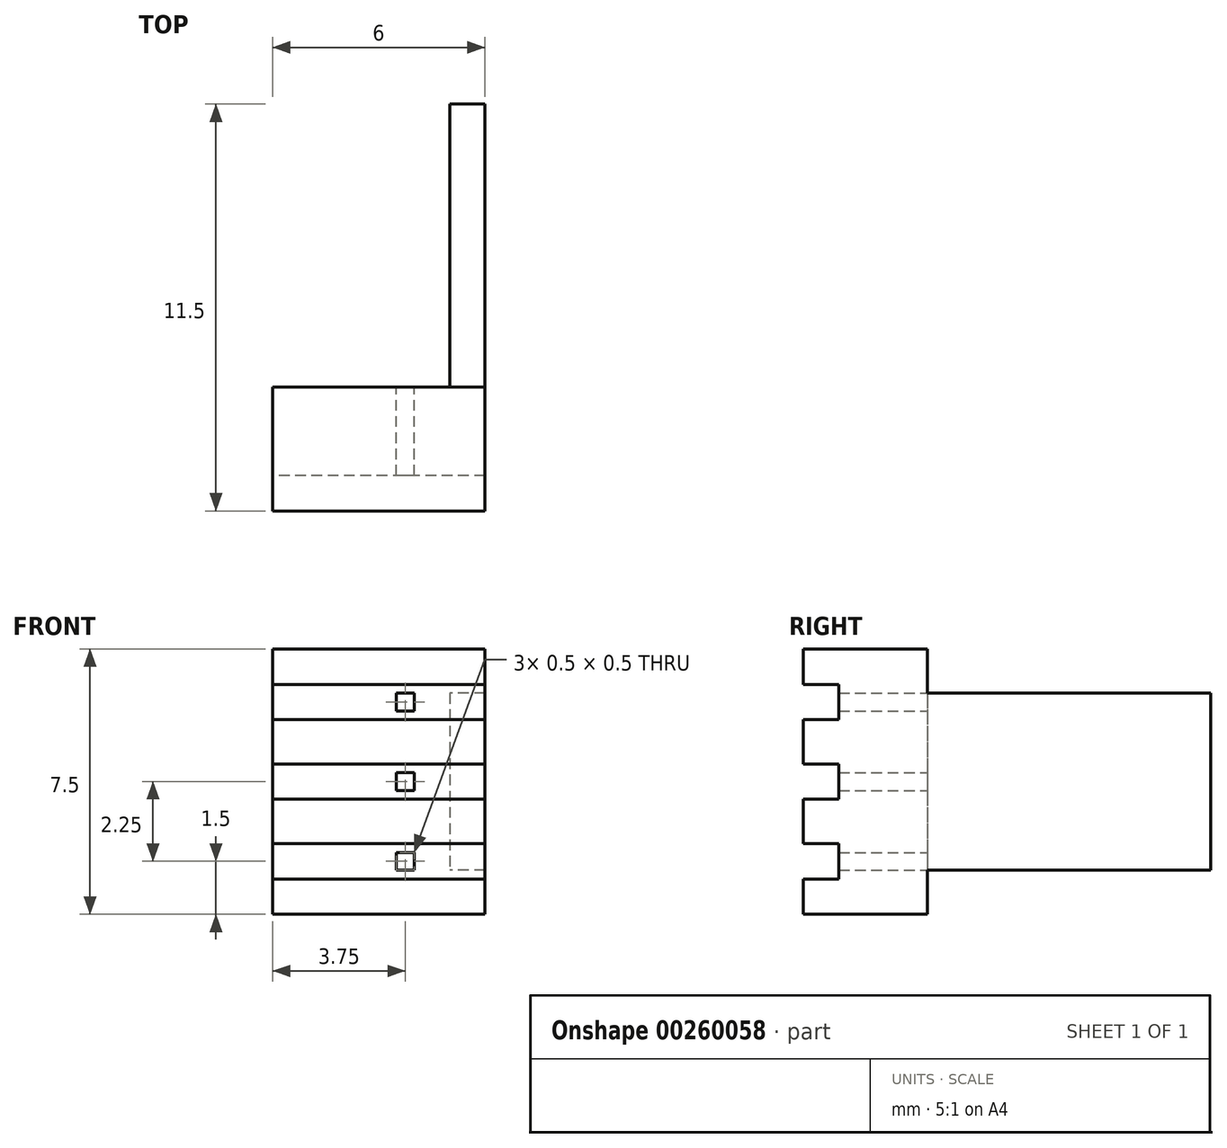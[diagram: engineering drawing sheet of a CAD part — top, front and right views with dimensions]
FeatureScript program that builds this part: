
annotation { "Feature Type Name" : "Feature", "Feature Type Description" : "" }
export const myFeature = defineFeature(function(context is Context, id is Id, definition is map)
    precondition{}
    {
        {
            var Q0;
            Q0=qCreatedBy(makeId("Top.planeOp"),FACE);
            var sketch = newSketch(context, id + "F0", { "sketchPlane" : qUnion([Q0])});
            skLineSegment(sketch, "E0.bottom", {"start": v(0, 0) * mm, "end": v(6, 0) * mm});
            skLineSegment(sketch, "E0.top", {"start": v(5, 11.5) * mm, "end": v(6, 11.5) * mm});
            skLineSegment(sketch, "E0.left", {"start": v(0, 0) * mm, "end": v(0, 3.5) * mm});
            skLineSegment(sketch, "E0.right", {"start": v(6, 0) * mm, "end": v(6, 11.5) * mm});
            skLineSegment(sketch, "E1", {"start": v(5, 11.5) * mm, "end": v(5, 3.5) * mm});
            skLineSegment(sketch, "E2", {"start": v(5, 3.5) * mm, "end": v(0, 3.5) * mm});
            skSolve(sketch);
        }
        {
            var Q0;
            Q0=qSketchRegion(id+"F0",true);
            extrude(context, id + "F1", {"entities" : qUnion([Q0]), "depth" : 7.5 * mm});
        }
        {
            var Q0;
            Q0=makeQuery(id+"F1.opExtrude","SWEPT_FACE",FACE,{"disambiguationData":[OSD([sQuery(id+"F0.wireOp",EDGE,"E1")])]});
            var sketch = newSketch(context, id + "F2", { "sketchPlane" : qUnion([Q0])});
            skLineSegment(sketch, "E3.bottom", {"start": v(-11.5, 0) * mm, "end": v(-3.5, 0) * mm});
            skLineSegment(sketch, "E3.top", {"start": v(-11.5, 1.25) * mm, "end": v(-3.5, 1.25) * mm});
            skLineSegment(sketch, "E3.left", {"start": v(-11.5, 0) * mm, "end": v(-11.5, 1.25) * mm});
            skLineSegment(sketch, "E3.right", {"start": v(-3.5, 0) * mm, "end": v(-3.5, 1.25) * mm});
            skLineSegment(sketch, "E4.bottom", {"start": v(-11.5, 7.5) * mm, "end": v(-3.5, 7.5) * mm});
            skLineSegment(sketch, "E4.top", {"start": v(-11.5, 6.25) * mm, "end": v(-3.5, 6.25) * mm});
            skLineSegment(sketch, "E4.left", {"start": v(-11.5, 7.5) * mm, "end": v(-11.5, 6.25) * mm});
            skLineSegment(sketch, "E4.right", {"start": v(-3.5, 7.5) * mm, "end": v(-3.5, 6.25) * mm});
            skSolve(sketch);
        }
        {
            var Q0;
            Q0=qSketchRegion(id+"F2",true);
            extrude(context, id + "F3", {"entities" : qUnion([Q0]), "operationType" : NewBodyOperationType.REMOVE, "oppositeDirection" : true, "depth" : 25 * mm});
        }
        {
            var Q0;
            Q0=makeQuery(id+"F3.boolean.opBoolean","MERGE",FACE,{"derivedFrom":[makeQuery(id+"F1.opExtrude","SWEPT_FACE",FACE,{"disambiguationData":[OSD([sQuery(id+"F0.wireOp",EDGE,"E2")])]}),makeQuery(id+"F3.opExtrude","SWEPT_FACE",FACE,{"disambiguationData":[OSD([sQuery(id+"F2.wireOp",EDGE,"E3.right")])]}),makeQuery(id+"F3.opExtrude","SWEPT_FACE",FACE,{"disambiguationData":[OSD([sQuery(id+"F2.wireOp",EDGE,"E4.right")])]})]});
            var sketch = newSketch(context, id + "F4", { "sketchPlane" : qUnion([Q0])});
            skLineSegment(sketch, "E5.bottom", {"start": v(-4, 6.25) * mm, "end": v(-3.5, 6.25) * mm});
            skLineSegment(sketch, "E5.top", {"start": v(-4, 1.25) * mm, "end": v(-3.5, 1.25) * mm});
            skLineSegment(sketch, "E5.left", {"start": v(-4, 6.25) * mm, "end": v(-4, 5.75) * mm});
            skLineSegment(sketch, "E5.right", {"start": v(-3.5, 6.25) * mm, "end": v(-3.5, 5.75) * mm});
            skLineSegment(sketch, "E6", {"start": v(-4, 5.75) * mm, "end": v(-3.5, 5.75) * mm});
            skLineSegment(sketch, "E7", {"start": v(-4, 1.75) * mm, "end": v(-3.5, 1.75) * mm});
            skLineSegment(sketch, "E8", {"start": v(-4, 4) * mm, "end": v(-3.5, 4) * mm});
            skLineSegment(sketch, "E9", {"start": v(-4, 3.5) * mm, "end": v(-3.5, 3.5) * mm});
            skLineSegment(sketch, "E10.trimOffspring", {"start": v(-4, 4) * mm, "end": v(-4, 3.5) * mm});
            skLineSegment(sketch, "E11.trimOffspring", {"start": v(-3.5, 4) * mm, "end": v(-3.5, 3.5) * mm});
            skLineSegment(sketch, "E12.trimOffspring", {"start": v(-4, 1.75) * mm, "end": v(-4, 1.25) * mm});
            skLineSegment(sketch, "E13.trimOffspring", {"start": v(-3.5, 1.75) * mm, "end": v(-3.5, 1.25) * mm});
            skLineSegment(sketch, "E14", {"start": v(0, 3.75) * mm, "end": v(-5, 3.75) * mm, "construction": true});
            skPoint(sketch, "E14.endSnap0", {"position": v(0, 3.75) * mm});
            skSolve(sketch);
        }
        {
            var Q0;
            Q0=qSketchRegion(id+"F4",true);
            var Q1;
            Q1=makeQuery(id+"F1.opExtrude","SWEPT_FACE",FACE,{"disambiguationData":[OSD([sQuery(id+"F0.wireOp",EDGE,"E0.top")])]});
            extrude(context, id + "F5", {"entities" : qUnion([Q0]), "operationType" : NewBodyOperationType.REMOVE, "oppositeDirection" : true, "endBoundEntityFace" : qUnion([Q1]), "depth" : 25 * mm});
        }
        {
            var Q0;
            Q0=makeQuery(id+"F1.opExtrude","SWEPT_FACE",FACE,{"disambiguationData":[OSD([sQuery(id+"F0.wireOp",EDGE,"E0.bottom")])]});
            var sketch = newSketch(context, id + "F6", { "sketchPlane" : qUnion([Q0])});
            skLineSegment(sketch, "E15.bottom", {"start": v(6, 6.5) * mm, "end": v(0, 6.5) * mm});
            skLineSegment(sketch, "E15.top", {"start": v(6, 5.5) * mm, "end": v(0, 5.5) * mm});
            skLineSegment(sketch, "E15.left", {"start": v(6, 6.5) * mm, "end": v(6, 5.5) * mm});
            skLineSegment(sketch, "E15.right", {"start": v(0, 6.5) * mm, "end": v(0, 5.5) * mm});
            skLineSegment(sketch, "E16.bottom", {"start": v(6, 4.25) * mm, "end": v(0, 4.25) * mm});
            skLineSegment(sketch, "E16.top", {"start": v(6, 3.25) * mm, "end": v(0, 3.25) * mm});
            skLineSegment(sketch, "E16.left", {"start": v(6, 4.25) * mm, "end": v(6, 3.25) * mm});
            skLineSegment(sketch, "E16.right", {"start": v(0, 4.25) * mm, "end": v(0, 3.25) * mm});
            skLineSegment(sketch, "E17.bottom", {"start": v(6, 2) * mm, "end": v(0, 2) * mm});
            skLineSegment(sketch, "E17.top", {"start": v(6, 1) * mm, "end": v(0, 1) * mm});
            skLineSegment(sketch, "E17.left", {"start": v(6, 2) * mm, "end": v(6, 1) * mm});
            skLineSegment(sketch, "E17.right", {"start": v(0, 2) * mm, "end": v(0, 1) * mm});
            skSolve(sketch);
        }
        {
            var Q0;
            Q0=qSketchRegion(id+"F6",true);
            extrude(context, id + "F7", {"entities" : qUnion([Q0]), "operationType" : NewBodyOperationType.REMOVE, "oppositeDirection" : true, "depth" : 1 * mm});
        }
    });
